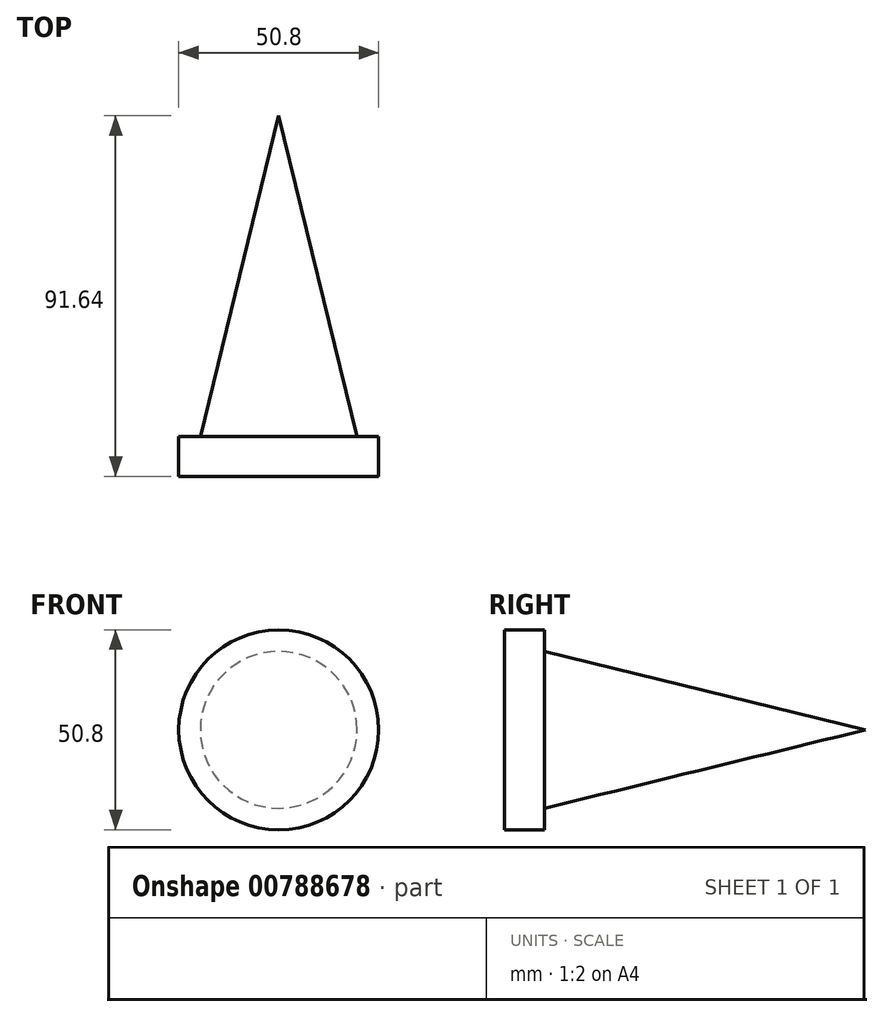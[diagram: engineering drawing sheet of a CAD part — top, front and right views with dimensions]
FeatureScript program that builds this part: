
annotation { "Feature Type Name" : "Feature", "Feature Type Description" : "" }
export const myFeature = defineFeature(function(context is Context, id is Id, definition is map)
    precondition{}
    {
        {
            var Q0;
            Q0=qCreatedBy(makeId("Front.planeOp"),FACE);
            var sketch = newSketch(context, id + "F0", { "sketchPlane" : qUnion([Q0])});
            skCircle(sketch, "E0", {"center": v(0, 0) * mm, "radius": 25.4 * mm});
            skSolve(sketch);
        }
        {
            var Q0;
            Q0 = qSketchRegion(id + "F0", true);
            extrude(context, id + "F1", {"entities" : qUnion([Q0]), "depth" : 10.16 * mm, "offsetDistance" : 25.4 * mm});
        }
        {
            var Q0;
            Q0=qCreatedBy(makeId("Top.planeOp"),FACE);
            var sketch = newSketch(context, id + "F2", { "sketchPlane" : qUnion([Q0])});
            skLineSegment(sketch, "E1", {"start": v(0, 0) * mm, "end": v(19.91, 0) * mm});
            skLineSegment(sketch, "E2", {"start": v(19.91, 0) * mm, "end": v(0, 81.48) * mm});
            skLineSegment(sketch, "E3", {"start": v(0, 81.48) * mm, "end": v(0, 0) * mm});
            skSolve(sketch);
        }
        {
            var Q0;
            Q0 = qSketchRegion(id + "F2", true);
            var Q1;
            Q1=makeQuery(id+"F1.opExtrude","CAP_EDGE",EDGE,{"disambiguationData":[OSD([sQuery(id+"F0.wireOp",EDGE,"E0")])],"isStart":true});
            revolve(context, id + "F3", {"operationType" : NewBodyOperationType.ADD, "surfaceOperationType" : NewSurfaceOperationType.NEW, "entities" : qUnion([Q0]), "axis" : qUnion([Q1]), "revolveType" : RevolveType.FULL});
        }
    });
